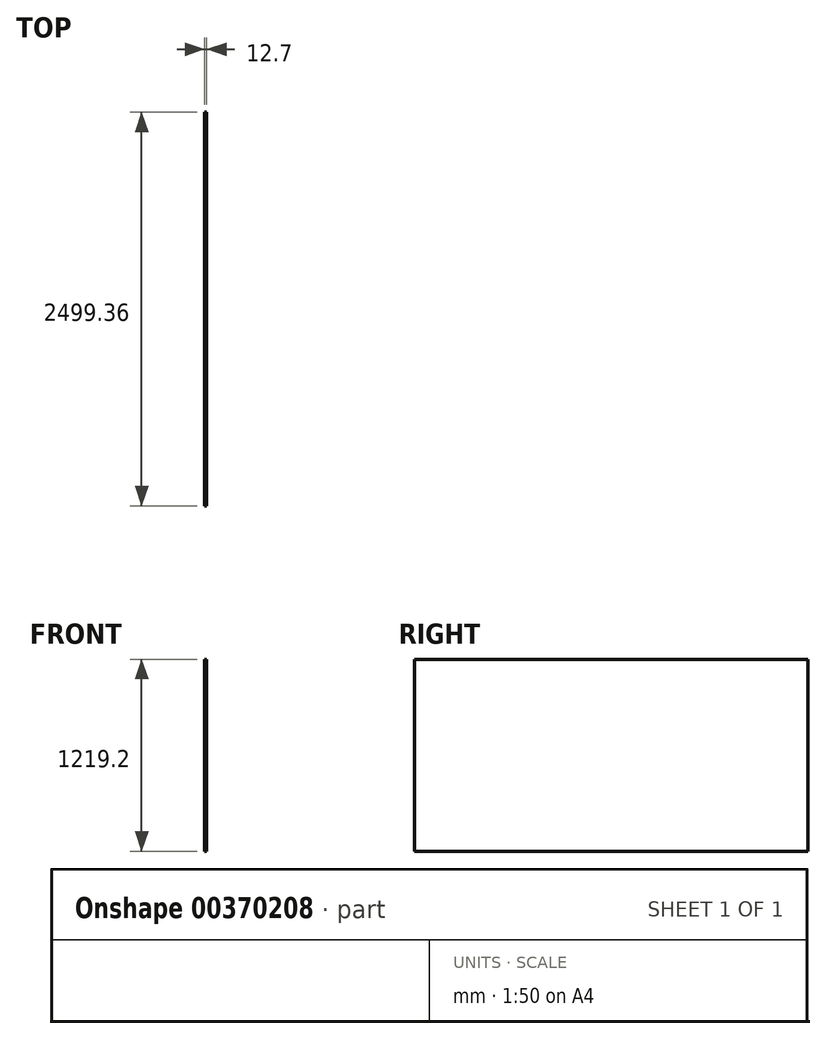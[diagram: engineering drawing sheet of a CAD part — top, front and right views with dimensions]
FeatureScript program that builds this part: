
annotation { "Feature Type Name" : "Feature", "Feature Type Description" : "" }
export const myFeature = defineFeature(function(context is Context, id is Id, definition is map)
    precondition{}
    {
        {
            var Q0;
            Q0=qCreatedBy(makeId("Right.planeOp"),FACE);
            var sketch = newSketch(context, id + "F0", { "sketchPlane" : qUnion([Q0])});
            skLineSegment(sketch, "E0.bottom", {"start": v(-1195.58, 644.4) * mm, "end": v(1242.82, 644.4) * mm});
            skLineSegment(sketch, "E0.top", {"start": v(-1195.58, -574.8) * mm, "end": v(1242.82, -574.8) * mm});
            skLineSegment(sketch, "E0.left", {"start": v(-1195.58, 644.4) * mm, "end": v(-1195.58, -574.8) * mm});
            skLineSegment(sketch, "E0.right", {"start": v(1242.82, 644.4) * mm, "end": v(1242.82, -574.8) * mm});
            skSolve(sketch);
        }
        {
            var Q0;
            Q0=makeQuery(id+"F0.imprint","IMPRINT",FACE,{"disambiguationData":[TD([[makeQuery(id+"F0.imprint","IMPRINT",EDGE,{"derivedFrom":sQuery(id+"F0.wireOp",EDGE,"E0.bottom")}),-1.0]])]});
            extrude(context, id + "F1", {"entities" : qUnion([Q0]), "depth" : 12.7 * mm});
        }
        {
            var Q0;
            Q0=makeQuery(id+"F1.opExtrude","SWEPT_FACE",FACE,{"disambiguationData":[OSD([sQuery(id+"F0.wireOp",EDGE,"E0.right")])]});
            extrude(context, id + "F2", {"entities" : qUnion([Q0]), "operationType" : NewBodyOperationType.ADD, "depth" : 45.72 * mm});
        }
        {
            var Q0;
            Q0=makeQuery(id+"F1.opExtrude","SWEPT_FACE",FACE,{"disambiguationData":[OSD([sQuery(id+"F0.wireOp",EDGE,"E0.left")])]});
            extrude(context, id + "F3", {"entities" : qUnion([Q0]), "operationType" : NewBodyOperationType.ADD, "depth" : 15.24 * mm});
        }
    });
